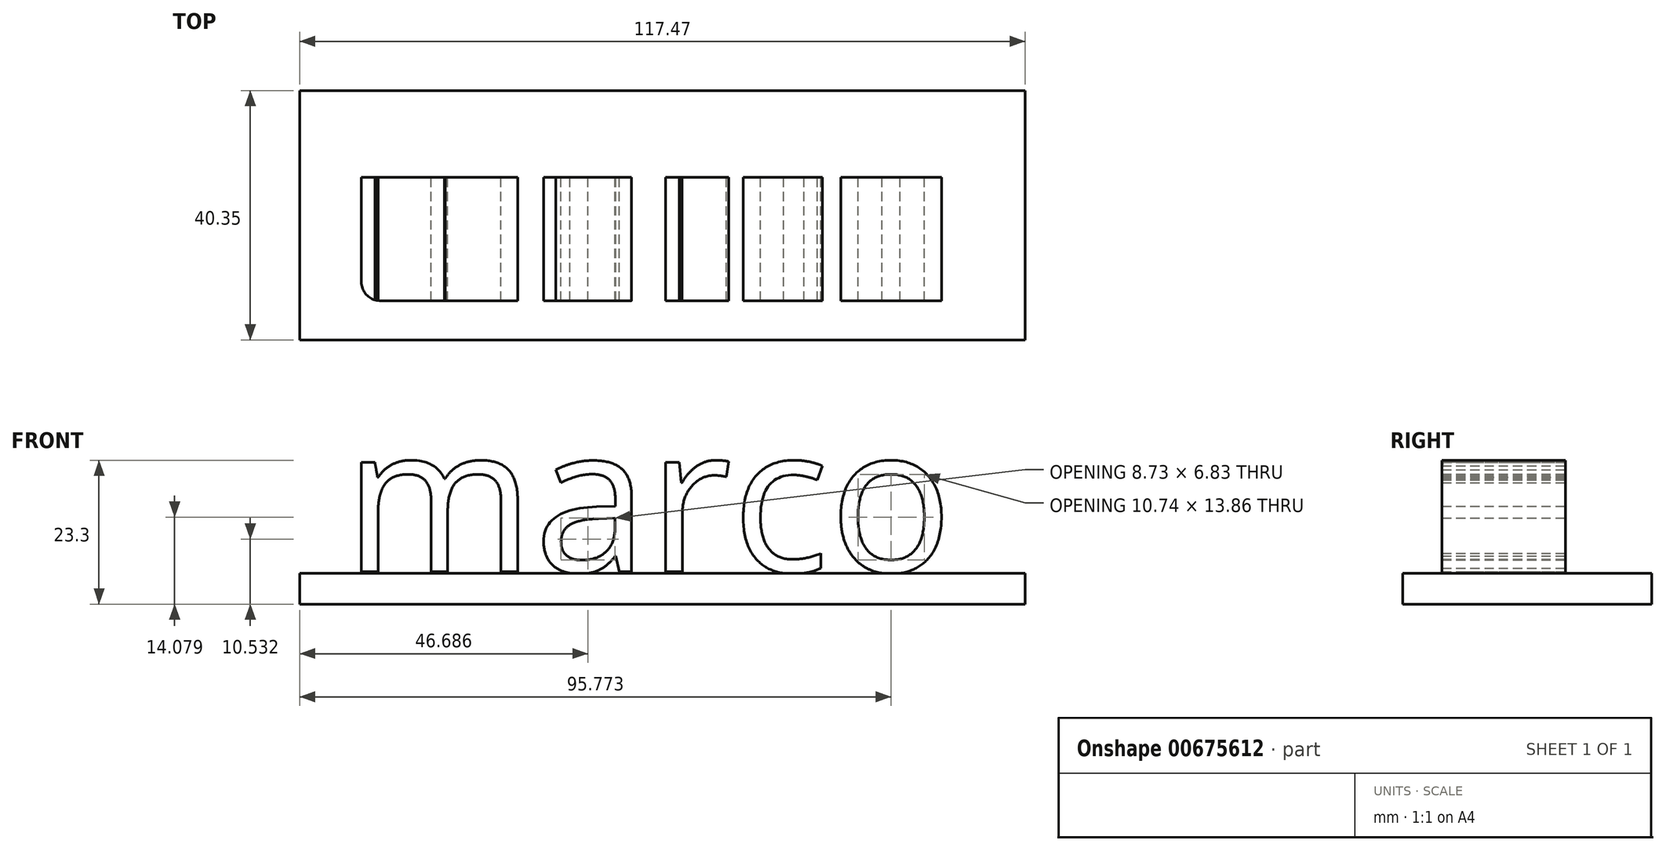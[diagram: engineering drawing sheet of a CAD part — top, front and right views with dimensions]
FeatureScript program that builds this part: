
annotation { "Feature Type Name" : "Feature", "Feature Type Description" : "" }
export const myFeature = defineFeature(function(context is Context, id is Id, definition is map)
    precondition{}
    {
        {
            var Q0;
            Q0=qCreatedBy(makeId("Top.planeOp"),FACE);
            var sketch = newSketch(context, id + "F0", { "sketchPlane" : qUnion([Q0])});
            skLineSegment(sketch, "E0.bottom", {"start": v(-56.95, 14) * mm, "end": v(60.52, 14) * mm});
            skLineSegment(sketch, "E0.top", {"start": v(-56.95, -26.35) * mm, "end": v(60.52, -26.35) * mm});
            skLineSegment(sketch, "E0.left", {"start": v(-56.95, 14) * mm, "end": v(-56.95, -26.35) * mm});
            skLineSegment(sketch, "E0.right", {"start": v(60.52, 14) * mm, "end": v(60.52, -26.35) * mm});
            skSolve(sketch);
        }
        {
            var Q0;
            Q0=makeQuery(id+"F0.imprint","IMPRINT",FACE,{"disambiguationData":[TD([[makeQuery(id+"F0.imprint","IMPRINT",EDGE,{"derivedFrom":sQuery(id+"F0.wireOp",EDGE,"E0.bottom")}),-1.0]])]});
            extrude(context, id + "F1", {"entities" : qUnion([Q0]), "depth" : 5 * mm, "offsetDistance" : 25.4 * mm});
        }
        {
            var Q0;
            Q0=qCreatedBy(makeId("Front.planeOp"),FACE);
            var sketch = newSketch(context, id + "F2", { "sketchPlane" : qUnion([Q0])});
            skText(sketch, "E1", { "text": "marco", "fontName": "OpenSans-Regular.ttf"});
            const initialGuessF2  = {"E1": [-0.04982, 0.00522, 1, 0, 0.02388]};
            skSetInitialGuess(sketch, initialGuessF2);
            skSolve(sketch);
        }
        {
            var Q0;
            Q0 = qSketchRegion(id + "F2", true);
            extrude(context, id + "F3", {"entities" : qUnion([Q0]), "operationType" : NewBodyOperationType.ADD, "depth" : 20 * mm, "offsetDistance" : 25.4 * mm});
        }
        {
            var Q0;
            Q0=makeQuery(id+"F3.opExtrude","CAP_EDGE",EDGE,{"disambiguationData":[OSD([sQuery(id+"F2.wireOp",EDGE,"E1.sketch_text.stroke-14")])],"isStart":false});
            fillet(context, id + "F4", {"entities" : qUnion([Q0]), "radius" : 3 * mm, "tangentPropagation" : true, "allowEdgeOverflow" : false});
        }
    });
